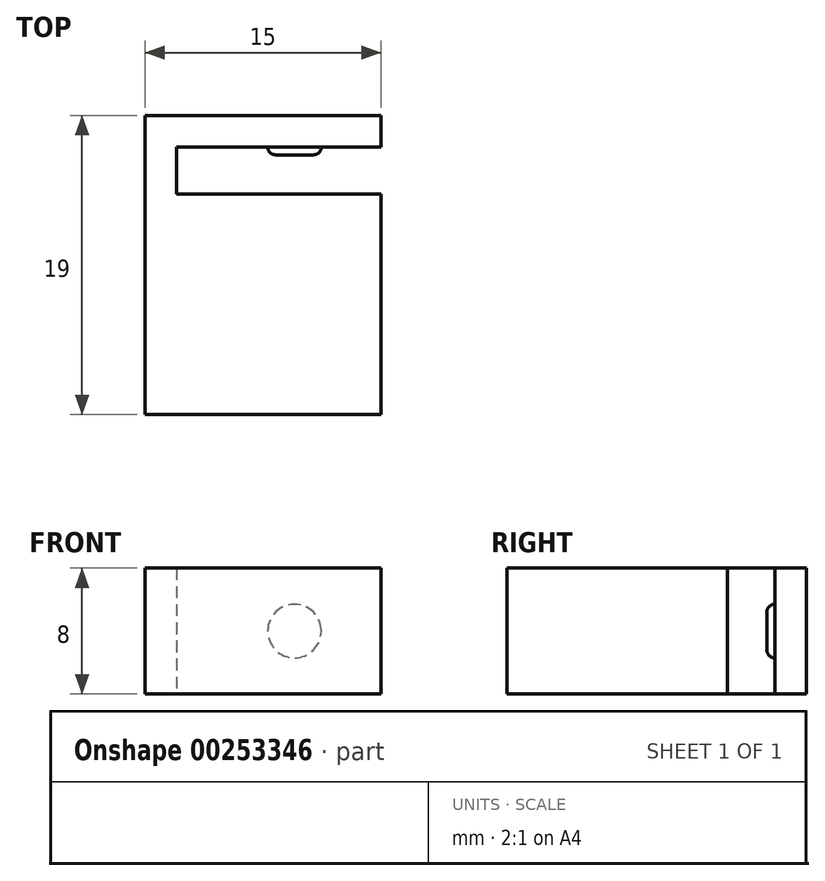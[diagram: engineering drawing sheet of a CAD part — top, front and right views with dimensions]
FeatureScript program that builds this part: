
annotation { "Feature Type Name" : "Feature", "Feature Type Description" : "" }
export const myFeature = defineFeature(function(context is Context, id is Id, definition is map)
    precondition{}
    {
        {
            var Q0;
            Q0=qCreatedBy(makeId("Top.planeOp"),FACE);
            var sketch = newSketch(context, id + "F0", { "sketchPlane" : qUnion([Q0])});
            skLineSegment(sketch, "E0.bottom", {"start": v(7.5, -9.5) * mm, "end": v(-7.5, -9.5) * mm});
            skLineSegment(sketch, "E0.top", {"start": v(7.5, 9.5) * mm, "end": v(-7.5, 9.5) * mm});
            skLineSegment(sketch, "E0.left", {"start": v(7.5, -9.5) * mm, "end": v(7.5, 9.5) * mm});
            skLineSegment(sketch, "E0.right", {"start": v(-7.5, -9.5) * mm, "end": v(-7.5, 9.5) * mm});
            skPoint(sketch, "E0.middle", {"position": v(0, 0) * mm});
            skLineSegment(sketch, "E1.bottom", {"start": v(7.5, 7.5) * mm, "end": v(-5.5, 7.5) * mm});
            skLineSegment(sketch, "E1.top", {"start": v(7.5, 4.5) * mm, "end": v(-5.5, 4.5) * mm});
            skLineSegment(sketch, "E1.left", {"start": v(7.5, 7.5) * mm, "end": v(7.5, 4.5) * mm});
            skLineSegment(sketch, "E1.right", {"start": v(-5.5, 7.5) * mm, "end": v(-5.5, 4.5) * mm});
            skSolve(sketch);
        }
        {
            var Q0;
            {var subQ4=sQuery(id+"F0.wireOp",EDGE,"E0.bottom");Q0=makeQuery(id+"F0.imprint","IMPRINT",FACE,{"disambiguationData":[TD([[makeQuery(id+"F0.imprint","IMPRINT",EDGE,{"derivedFrom":subQ4}),-1.0]])]});}
            extrude(context, id + "F1", {"entities" : qUnion([Q0]), "depth" : 8 * mm});
        }
        {
            var Q0;
            Q0=makeQuery(id+"F1.opExtrude","SWEPT_FACE",FACE,{"disambiguationData":[OSD([sQuery(id+"F0.wireOp",EDGE,"E1.bottom")])]});
            var sketch = newSketch(context, id + "F2", { "sketchPlane" : qUnion([Q0])});
            skPoint(sketch, "E2.endSnap0", {"position": v(7.5, 4) * mm});
            skCircle(sketch, "E3", {"center": v(2, 4) * mm, "radius": 1.7 * mm});
            skLineSegment(sketch, "E4", {"start": v(-5.5, 4) * mm, "end": v(2, 4) * mm, "construction": true});
            skSolve(sketch);
        }
        {
            var Q0;
            Q0 = qSketchRegion(id + "F2", true);
            extrude(context, id + "F3", {"entities" : qUnion([Q0]), "operationType" : NewBodyOperationType.ADD, "depth" : .5 * mm});
        }
        {
            var Q0;
            Q0=makeQuery(id+"F3.opExtrude","CAP_EDGE",EDGE,{"disambiguationData":[OSD([sQuery(id+"F2.wireOp",EDGE,"E3")])],"isStart":false});
            fillet(context, id + "F4", {"entities" : qUnion([Q0]), "radius" : .5 * mm, "tangentPropagation" : true, "allowEdgeOverflow" : false});
        }
    });
